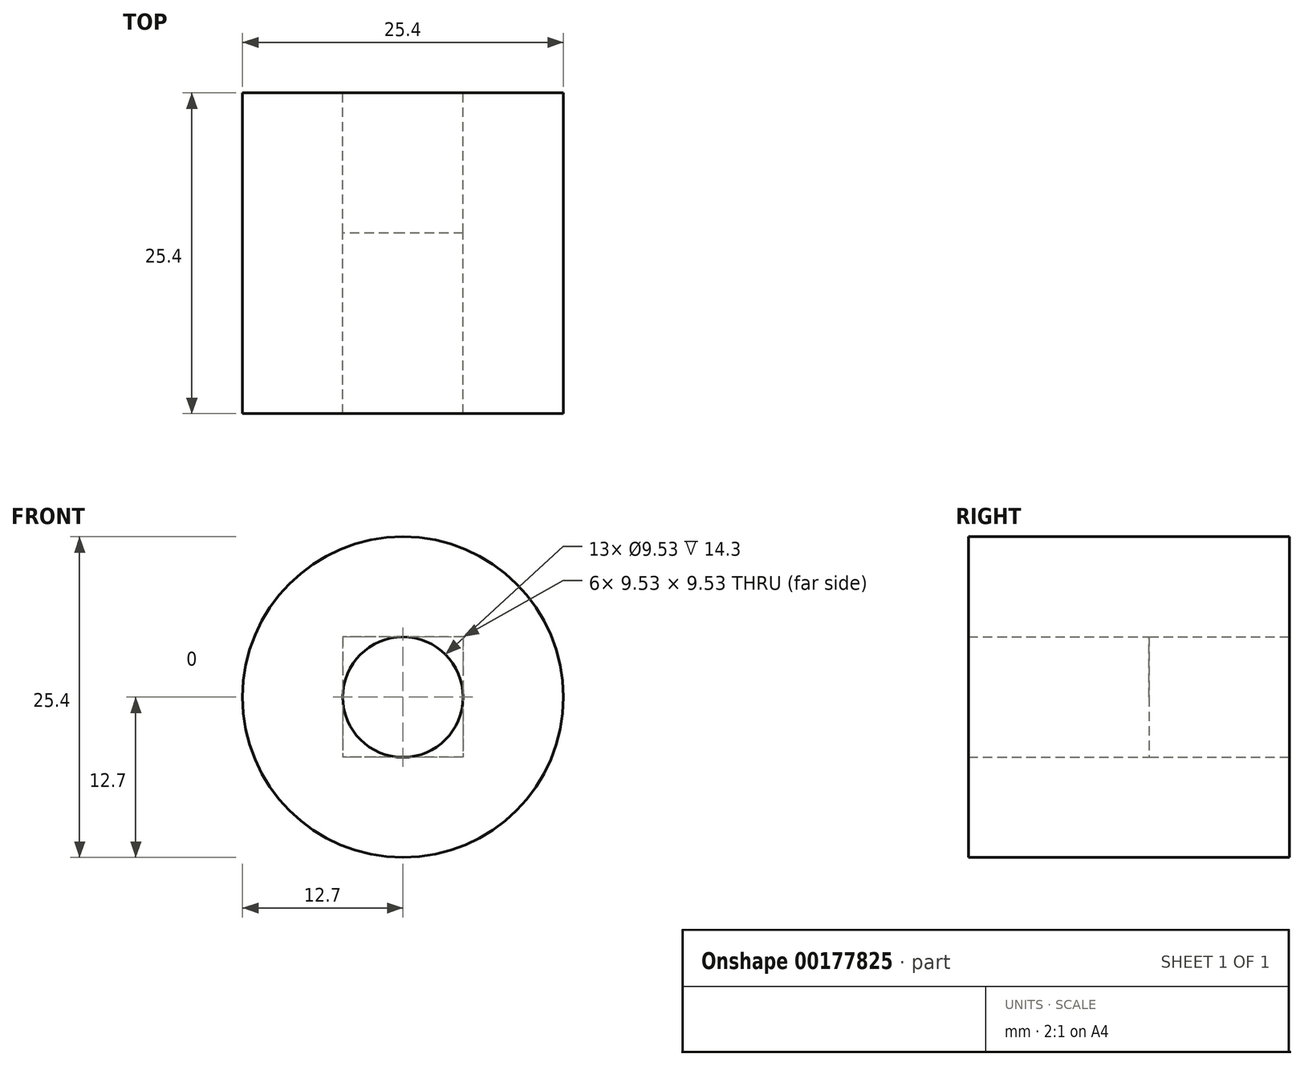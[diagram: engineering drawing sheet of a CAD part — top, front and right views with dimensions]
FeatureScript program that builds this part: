
annotation { "Feature Type Name" : "Feature", "Feature Type Description" : "" }
export const myFeature = defineFeature(function(context is Context, id is Id, definition is map)
    precondition{}
    {
        {
            var Q0;
            Q0=qCreatedBy(makeId("Front.planeOp"),FACE);
            var sketch = newSketch(context, id + "F0", { "sketchPlane" : qUnion([Q0])});
            skCircle(sketch, "E0", {"center": v(0, 0) * mm, "radius": 12.7 * mm});
            skSolve(sketch);
        }
        {
            var Q0;
            Q0 = qSketchRegion(id + "F0", true);
            extrude(context, id + "F1", {"entities" : qUnion([Q0]), "depth" : 25.4 * mm});
        }
        {
            var Q0;
            Q0=qCreatedBy(makeId("Front.planeOp"),FACE);
            var sketch = newSketch(context, id + "F2", { "sketchPlane" : qUnion([Q0])});
            skLineSegment(sketch, "E1.bottom", {"start": v(4.76, 4.76) * mm, "end": v(-4.76, 4.76) * mm});
            skLineSegment(sketch, "E1.top", {"start": v(4.76, -4.76) * mm, "end": v(-4.76, -4.76) * mm});
            skLineSegment(sketch, "E1.left", {"start": v(4.76, 4.76) * mm, "end": v(4.76, -4.76) * mm});
            skLineSegment(sketch, "E1.right", {"start": v(-4.76, 4.76) * mm, "end": v(-4.76, -4.76) * mm});
            skPoint(sketch, "E1.middle", {"position": v(0, 0) * mm});
            skCircle(sketch, "E2", {"center": v(0, 0) * mm, "radius": 4.76 * mm});
            skSolve(sketch);
        }
        {
            var Q0;
            Q0=makeQuery(id+"F1.opExtrude","CAP_FACE",FACE,{"disambiguationData":[OSD([sQuery(id+"F0.wireOp",EDGE,"E0")])],"isStart":false});
            extrude(context, id + "F3", {"entities" : qUnion([Q0]), "operationType" : NewBodyOperationType.REMOVE, "depth" : 25.4 * mm});
        }
        {
            var Q0;
            {var subQ0=sQuery(id+"F2.wireOp",EDGE,"E2");var subQ1=makeQuery(id+"F2.imprint","INTERSECT",VERTEX,{"derivedFrom":[sQuery(id+"F2.wireOp",EDGE,"E1.bottom"),subQ0]});Q0=makeQuery(id+"F2.imprint","IMPRINT",FACE,{"disambiguationData":[TD([[makeQuery(id+"F2.imprint","IMPRINT",EDGE,{"disambiguationData":[TD([[subQ1,1.0]])],"derivedFrom":subQ0}),1.0]])]});}
            extrude(context, id + "F4", {"entities" : qUnion([Q0]), "operationType" : NewBodyOperationType.REMOVE, "endBound" : BoundingType.THROUGH_ALL, "depth" : 25.4 * mm});
        }
        {
            var Q0;
            Q0 = qSketchRegion(id + "F2", true);
            extrude(context, id + "F5", {"entities" : qUnion([Q0]), "operationType" : NewBodyOperationType.REMOVE, "depth" : 11.1 * mm});
        }
    });
